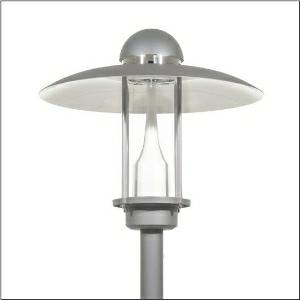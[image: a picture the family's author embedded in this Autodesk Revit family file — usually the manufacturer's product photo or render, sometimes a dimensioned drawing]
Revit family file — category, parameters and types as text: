
# Revit family: city-light_elegance_iq___st1_2a_5xa5265kf14hp_821b
name_source: partatom
category: Lighting Fixtures
units: mm (PartAtom-declared; Revit-internal decimal feet)

## family parameters
Cut with Voids When Loaded = No
Host = Face
Light Source = No
Part Type = Normal
Room Calculation Point = No
Round Connector Dimension = Use Diameter
Shared = No

## types (1)
- --- (1 x LED, 4720 lm, 33.6 W, 4000K)
    Apparent Load = 34 VA
    CIE Flux Codes = 22 61 93 98 100
    Color Rendering = 70
    Color Temperature = 4000K
    Default Elevation = 1800 mm
    Description = City-Light Elegance iQ, mast luminaire, Module 540 iQ-SR, primary light control with 3 zone facetted reflector, of plastic, silver coated, highly specular, structured, primary optical cover: cover, of PMMA, transparent, light distribution: ST1.2a, light emission: direct distribution, primary light characteristic: asymmetric, installation type: post-top, LED, High Power LED, rated luminous flux: 4.720lm, luminous efficacy: 141lm/W, light colour: 740, colour temperature: 4000K, control gear: iQ Street-Remote, control: pre-setting: logarithmic dimming characteristic, Street-Remote, Auto-Match, Temp-Guard, Lumen-Switch, Night-Set, Smart-Wire, Light-Fading, Desk-Remote (wireless, voltage-free reading and setting of iQ features in the workshop via application-optimized NFC function/RFID function), optimised constant luminous flux control (CLO 2.0), with terminal, 6-pole, max. 2.5mm², mains connection: 230..240V, AC, 50/60Hz, start of lifetime: 34W, end of service life: 36W, reduction: 15W, luminaire housing, upper part, of aluminium, coated, Siteco® metallic grey (DB 702S), diameter: 750mm, height: 675mm, spigot size: d x l = 76 x 70mm (post-top) | with reducer (optional accessory) 60 x 70mm, mounting height: 3..5m, post-top mast mounting element, of diecast aluminium, coated, Siteco® metallic grey (DB 702S), Module 540 iQ-SR, traffic white (RAL 9016), equipment: Power, protection rating (complete): IP65, insulation class (complete): insulation class II (safety insulation), certification: CE, ENEC, VDE, packaging unit: 1 piece

Light Distribution: ST1.2a
    Height = 675 mm
    Lamp = 1 x LED
    Lamp Light Flux = 4720 lm
    Lamp Power = 33.6 W
    Lamp count = 1
    Length = 750 mm
    Luminous efficacy = 140 lm/W
    Manufacturer = Siteco
    ModVariant = No
    Model = 5XA5265KF14HP
    Number of Poles = 1
    OnlyDefault = Yes
    Power Factor = 1
    Product Name = City-Light Elegance iQ | ST1.2a
    Product group = mast luminaire | pylon top
    ProductGroupID = 6100
    Protection Class = Protection class II
    Protection Degree = IP 65
    RLX_Detail_Level = 1
    RLX_Emergency_Light_Flux = 0 lm
    RLX_Emergency_Type = 0
    RLX_Emergency_Type_DB = No
    RlxData = <blob elided: 36617 chars, md5=65e523e8>
    Socket = socket
    Standby Power = 0 W
    System Light Flux = 4720 lm
    System Power = 34 W
    Type Comments = factory setting: luminous flux: 100 % | dim-lin: 254 | 695 mA
    Type Image = l_1006912.jpg
    URL = http://relux.com
    VarID = @adj_193012
    Voltage = 0 V
    Weight = 0.00 kg
    Width = 0 mm  [stored 0 ft]

note: [stored X ft] marks values corroborated as IEEE doubles in the binary element streams (Revit-internal decimal feet)

## geometry (parser evidence)
native form markers: Blend x4, Sweep x9
no freeform markers — native parametric forms only
